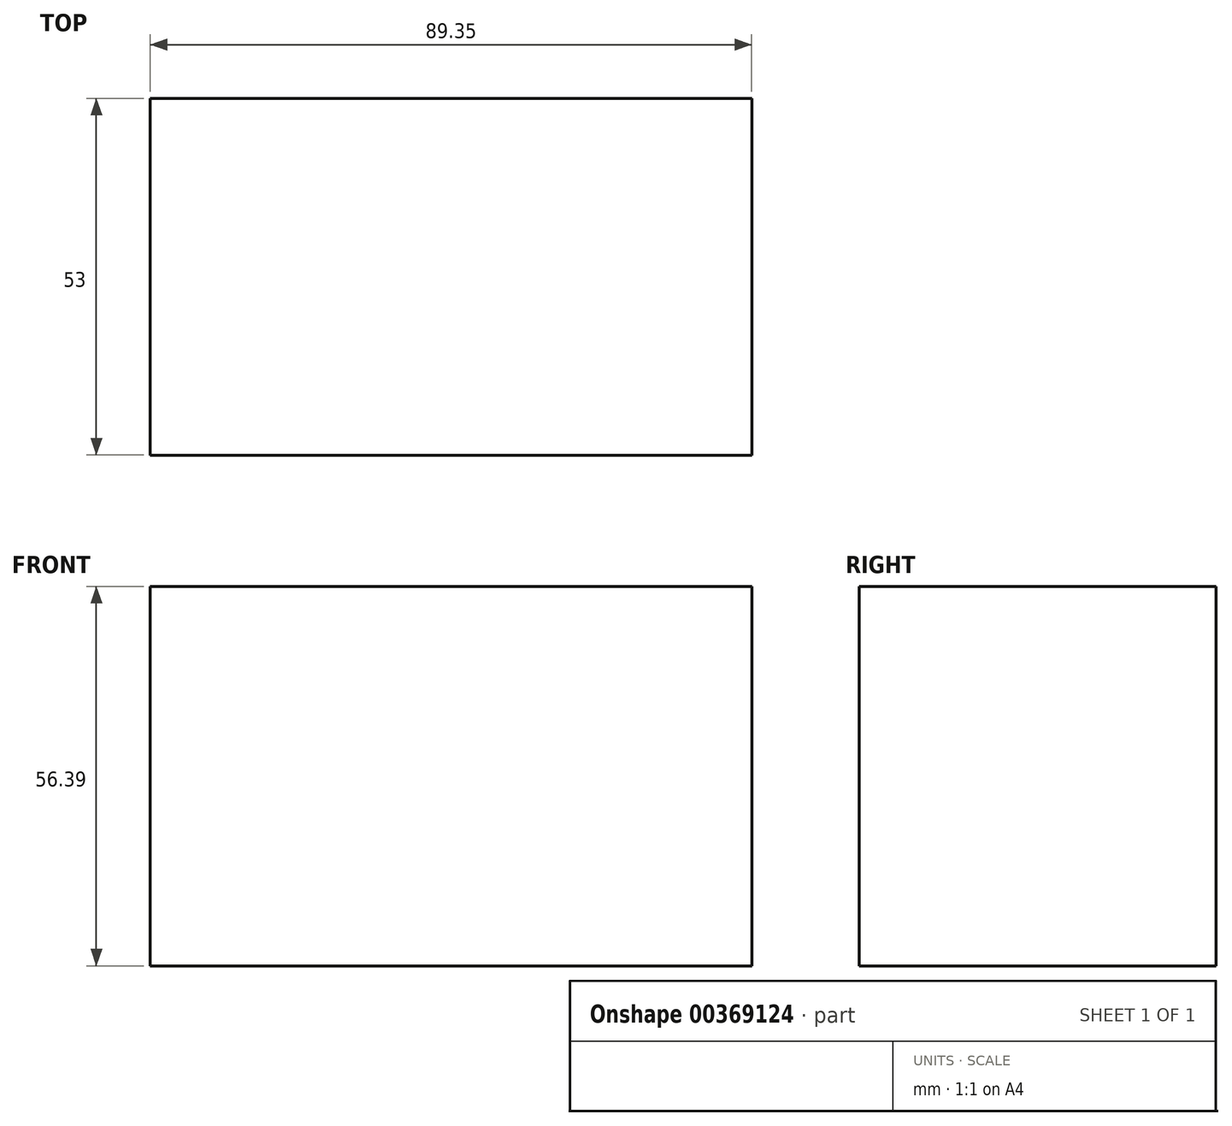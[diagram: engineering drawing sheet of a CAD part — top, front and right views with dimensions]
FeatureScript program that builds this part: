
annotation { "Feature Type Name" : "Feature", "Feature Type Description" : "" }
export const myFeature = defineFeature(function(context is Context, id is Id, definition is map)
    precondition{}
    {
        {
            var Q0;
            Q0=qCreatedBy(makeId("Top.planeOp"),FACE);
            var sketch = newSketch(context, id + "F0", { "sketchPlane" : qUnion([Q0])});
            skLineSegment(sketch, "E0.bottom", {"start": v(-46.85, 35.72) * mm, "end": v(42.5, 35.72) * mm});
            skLineSegment(sketch, "E0.top", {"start": v(-46.85, -17.28) * mm, "end": v(42.5, -17.28) * mm});
            skLineSegment(sketch, "E0.left", {"start": v(-46.85, 35.72) * mm, "end": v(-46.85, -17.28) * mm});
            skLineSegment(sketch, "E0.right", {"start": v(42.5, 35.72) * mm, "end": v(42.5, -17.28) * mm});
            skSolve(sketch);
        }
        {
            var Q0;
            Q0=makeQuery(id+"F0.imprint","IMPRINT",FACE,{"disambiguationData":[TD([[makeQuery(id+"F0.imprint","IMPRINT",EDGE,{"derivedFrom":sQuery(id+"F0.wireOp",EDGE,"E0.bottom")}),-1.0]])]});
            extrude(context, id + "F1", {"entities" : qUnion([Q0]), "oppositeDirection" : true, "depth" : 56.4 * mm});
        }
    });
